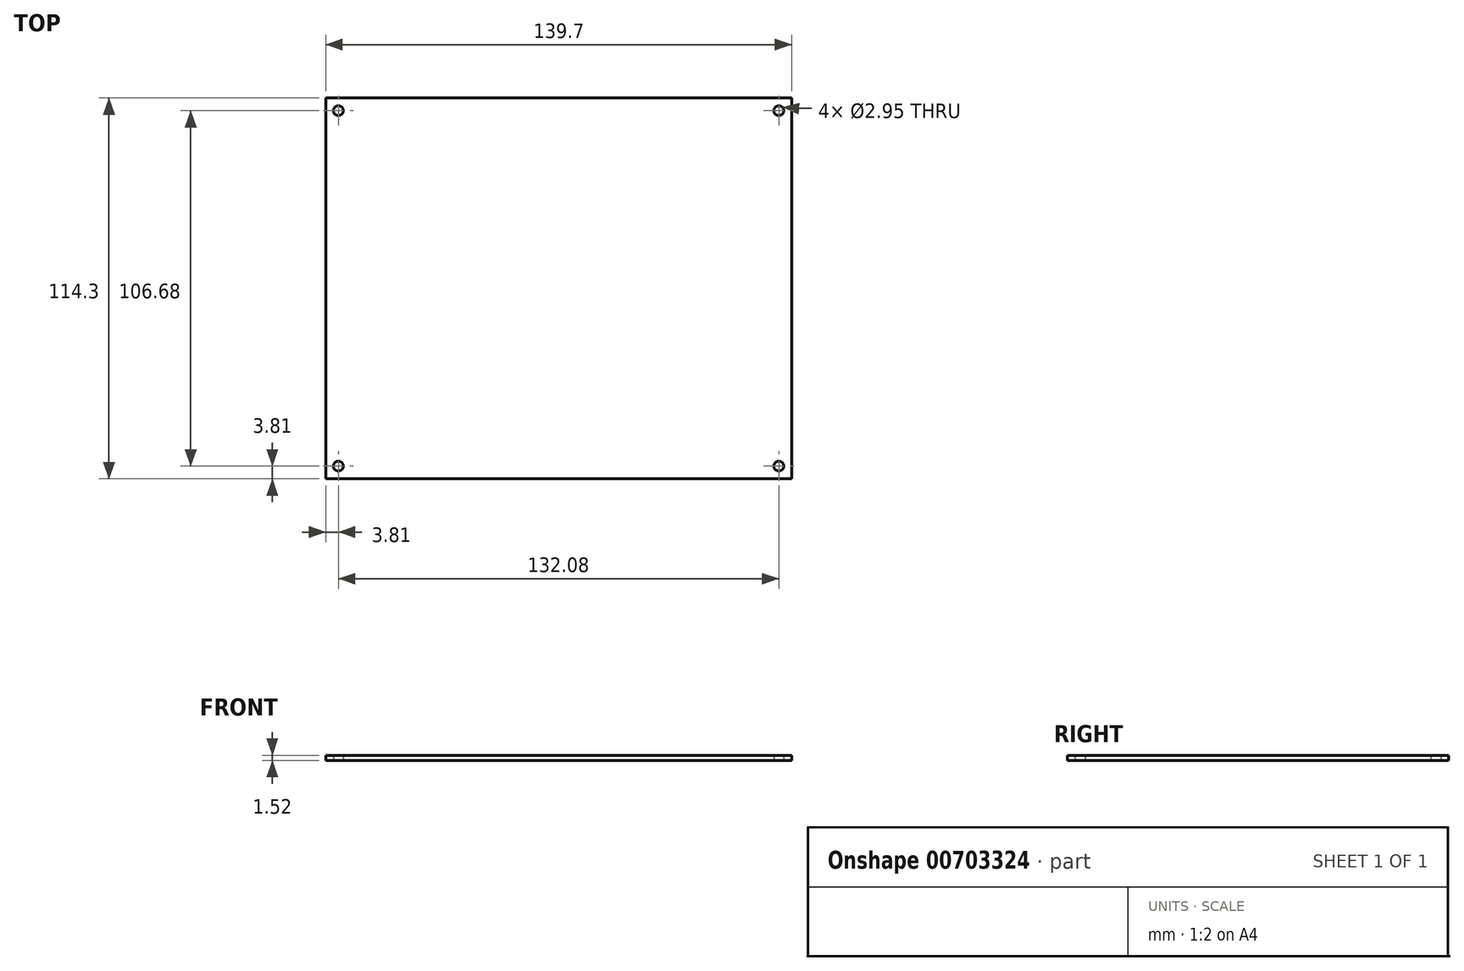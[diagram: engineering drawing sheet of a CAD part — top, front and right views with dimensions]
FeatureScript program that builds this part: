
annotation { "Feature Type Name" : "Feature", "Feature Type Description" : "" }
export const myFeature = defineFeature(function(context is Context, id is Id, definition is map)
    precondition{}
    {
        {
            var Q0;
            Q0=qCreatedBy(makeId("Top.planeOp"),FACE);
            var sketch = newSketch(context, id + "F0", { "sketchPlane" : qUnion([Q0])});
            skLineSegment(sketch, "E0.bottom", {"start": v(-69.85, -57.15) * mm, "end": v(69.85, -57.15) * mm});
            skLineSegment(sketch, "E0.top", {"start": v(-69.85, 57.15) * mm, "end": v(69.85, 57.15) * mm});
            skLineSegment(sketch, "E0.left", {"start": v(-69.85, -57.15) * mm, "end": v(-69.85, 57.15) * mm});
            skLineSegment(sketch, "E0.right", {"start": v(69.85, -57.15) * mm, "end": v(69.85, 57.15) * mm});
            skPoint(sketch, "E0.middle", {"position": v(0, 0) * mm});
            skCircle(sketch, "E1", {"center": v(-66.04, 53.34) * mm, "radius": 1.47 * mm});
            skCircle(sketch, "E2", {"center": v(66.04, 53.34) * mm, "radius": 1.47 * mm});
            skCircle(sketch, "E3", {"center": v(66.04, -53.34) * mm, "radius": 1.47 * mm});
            skCircle(sketch, "E4", {"center": v(-66.04, -53.34) * mm, "radius": 1.47 * mm});
            skSolve(sketch);
        }
        {
            var Q0;
            Q0=makeQuery(id+"F0.imprint","IMPRINT",FACE,{"disambiguationData":[TD([[makeQuery(id+"F0.imprint","IMPRINT",EDGE,{"derivedFrom":sQuery(id+"F0.wireOp",EDGE,"E0.bottom")}),1.0]])]});
            extrude(context, id + "F1", {"entities" : qUnion([Q0]), "depth" : 1.52 * mm, "offsetDistance" : 25 * mm});
        }
    });
